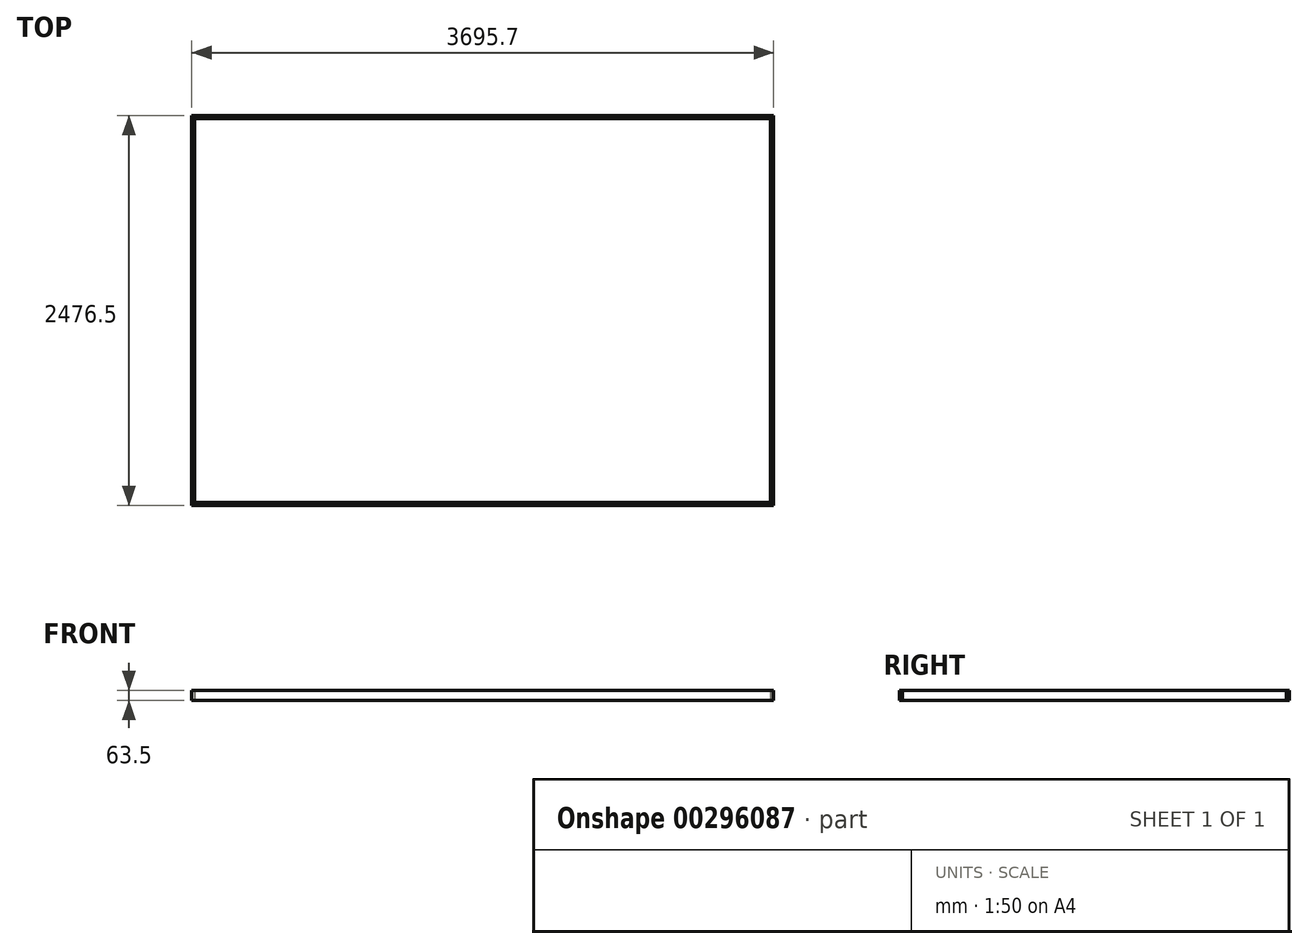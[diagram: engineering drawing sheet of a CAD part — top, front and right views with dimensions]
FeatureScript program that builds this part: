
annotation { "Feature Type Name" : "Feature", "Feature Type Description" : "" }
export const myFeature = defineFeature(function(context is Context, id is Id, definition is map)
    precondition{}
    {
        {
            var Q0;
            Q0=qCreatedBy(makeId("Top.planeOp"),FACE);
            var sketch = newSketch(context, id + "F0", { "sketchPlane" : qUnion([Q0])});
            skLineSegment(sketch, "E0.bottom", {"start": v(1828.8, 1219.2) * mm, "end": v(-1828.8, 1219.2) * mm});
            skLineSegment(sketch, "E0.top", {"start": v(1828.8, -1219.2) * mm, "end": v(-1828.8, -1219.2) * mm});
            skLineSegment(sketch, "E0.left", {"start": v(1828.8, 1219.2) * mm, "end": v(1828.8, -1219.2) * mm});
            skLineSegment(sketch, "E0.right", {"start": v(-1828.8, 1219.2) * mm, "end": v(-1828.8, -1219.2) * mm});
            skPoint(sketch, "E0.middle", {"position": v(0, 0) * mm});
            skSolve(sketch);
        }
        {
            var Q0;
            Q0=makeQuery(id+"F0.imprint","IMPRINT",FACE,{"disambiguationData":[TD([[makeQuery(id+"F0.imprint","IMPRINT",EDGE,{"derivedFrom":sQuery(id+"F0.wireOp",EDGE,"E0.bottom")}),1.0]])]});
            var sketch = newSketch(context, id + "F1", { "sketchPlane" : qUnion([Q0])});
            skLineSegment(sketch, "E1", {"start": v(-1828.8, 1219.2) * mm, "end": v(-1847.85, 1219.2) * mm});
            skLineSegment(sketch, "E2", {"start": v(-1847.85, 1219.2) * mm, "end": v(-1847.85, -1219.2) * mm});
            skLineSegment(sketch, "E3", {"start": v(-1847.85, -1219.2) * mm, "end": v(-1828.8, -1219.2) * mm});
            skSolve(sketch);
        }
        {
            var Q0;
            Q0=makeQuery(id+"F1.imprint","IMPRINT",FACE,{"disambiguationData":[TD([[makeQuery(id+"F1.imprint","IMPRINT",EDGE,{"derivedFrom":sQuery(id+"F1.wireOp",EDGE,"E1")}),1.0]])]});
            extrude(context, id + "F2", {"entities" : qUnion([Q0]), "depth" : 63.5 * mm});
        }
        {
            var Q0;
            Q0=makeQuery(id+"F0.imprint","IMPRINT",FACE,{"disambiguationData":[TD([[makeQuery(id+"F0.imprint","IMPRINT",EDGE,{"derivedFrom":sQuery(id+"F0.wireOp",EDGE,"E0.bottom")}),1.0]])]});
            var sketch = newSketch(context, id + "F3", { "sketchPlane" : qUnion([Q0])});
            skLineSegment(sketch, "E4", {"start": v(1828.8, 1219.2) * mm, "end": v(1847.85, 1219.2) * mm});
            skLineSegment(sketch, "E5", {"start": v(1847.85, 1219.2) * mm, "end": v(1847.85, -1219.2) * mm});
            skLineSegment(sketch, "E6", {"start": v(1847.85, -1219.2) * mm, "end": v(1828.8, -1219.2) * mm});
            skSolve(sketch);
        }
        {
            var Q0;
            Q0=makeQuery(id+"F3.imprint","IMPRINT",FACE,{"disambiguationData":[TD([[makeQuery(id+"F3.imprint","IMPRINT",EDGE,{"derivedFrom":sQuery(id+"F3.wireOp",EDGE,"E4")}),-1.0]])]});
            extrude(context, id + "F4", {"entities" : qUnion([Q0]), "depth" : 63.5 * mm});
        }
        {
            var Q0;
            Q0=makeQuery(id+"F0.imprint","IMPRINT",FACE,{"disambiguationData":[TD([[makeQuery(id+"F0.imprint","IMPRINT",EDGE,{"derivedFrom":sQuery(id+"F0.wireOp",EDGE,"E0.bottom")}),1.0]])]});
            var sketch = newSketch(context, id + "F5", { "sketchPlane" : qUnion([Q0])});
            skPoint(sketch, "E7", {"position": v(-1847.85, 1219.2) * mm});
            skLineSegment(sketch, "E8", {"start": v(-1847.85, 1219.2) * mm, "end": v(-1847.85, 1238.25) * mm});
            skLineSegment(sketch, "E9", {"start": v(-1847.85, 1238.25) * mm, "end": v(1847.85, 1238.25) * mm});
            skLineSegment(sketch, "E10", {"start": v(1847.85, 1238.25) * mm, "end": v(1847.85, 1219.2) * mm});
            skPoint(sketch, "E11", {"position": v(1847.85, 1219.2) * mm});
            skLineSegment(sketch, "E12", {"start": v(-1847.85, 1219.2) * mm, "end": v(1847.85, 1219.2) * mm});
            skSolve(sketch);
        }
        {
            var Q0;
            {var subQ2=sQuery(id+"F5.wireOp",EDGE,"E8");Q0=makeQuery(id+"F5.imprint","IMPRINT",FACE,{"disambiguationData":[TD([[makeQuery(id+"F5.imprint","IMPRINT",EDGE,{"derivedFrom":subQ2}),-1.0]])]});}
            extrude(context, id + "F6", {"entities" : qUnion([Q0]), "depth" : 63.5 * mm});
        }
        {
            var Q0;
            Q0=makeQuery(id+"F0.imprint","IMPRINT",FACE,{"disambiguationData":[TD([[makeQuery(id+"F0.imprint","IMPRINT",EDGE,{"derivedFrom":sQuery(id+"F0.wireOp",EDGE,"E0.bottom")}),1.0]])]});
            var sketch = newSketch(context, id + "F7", { "sketchPlane" : qUnion([Q0])});
            skLineSegment(sketch, "E13", {"start": v(-1847.85, -1219.2) * mm, "end": v(-1847.85, -1238.25) * mm});
            skLineSegment(sketch, "E14", {"start": v(-1847.85, -1238.25) * mm, "end": v(1847.85, -1238.25) * mm});
            skLineSegment(sketch, "E15", {"start": v(1847.85, -1238.25) * mm, "end": v(1847.85, -1219.2) * mm});
            skLineSegment(sketch, "E16", {"start": v(1847.85, -1219.2) * mm, "end": v(-1847.85, -1219.2) * mm});
            skSolve(sketch);
        }
        {
            var Q0;
            {var subQ3=sQuery(id+"F7.wireOp",EDGE,"E13");Q0=makeQuery(id+"F7.imprint","IMPRINT",FACE,{"disambiguationData":[TD([[makeQuery(id+"F7.imprint","IMPRINT",EDGE,{"derivedFrom":subQ3}),1.0]])]});}
            extrude(context, id + "F8", {"entities" : qUnion([Q0]), "depth" : 63.5 * mm});
        }
        {
            var Q0;
            Q0=makeQuery(id+"F0.imprint","IMPRINT",FACE,{"disambiguationData":[TD([[makeQuery(id+"F0.imprint","IMPRINT",EDGE,{"derivedFrom":sQuery(id+"F0.wireOp",EDGE,"E0.bottom")}),1.0]])]});
            extrude(context, id + "F9", {"entities" : qUnion([Q0]), "depth" : 0.25 * mm});
        }
    });
